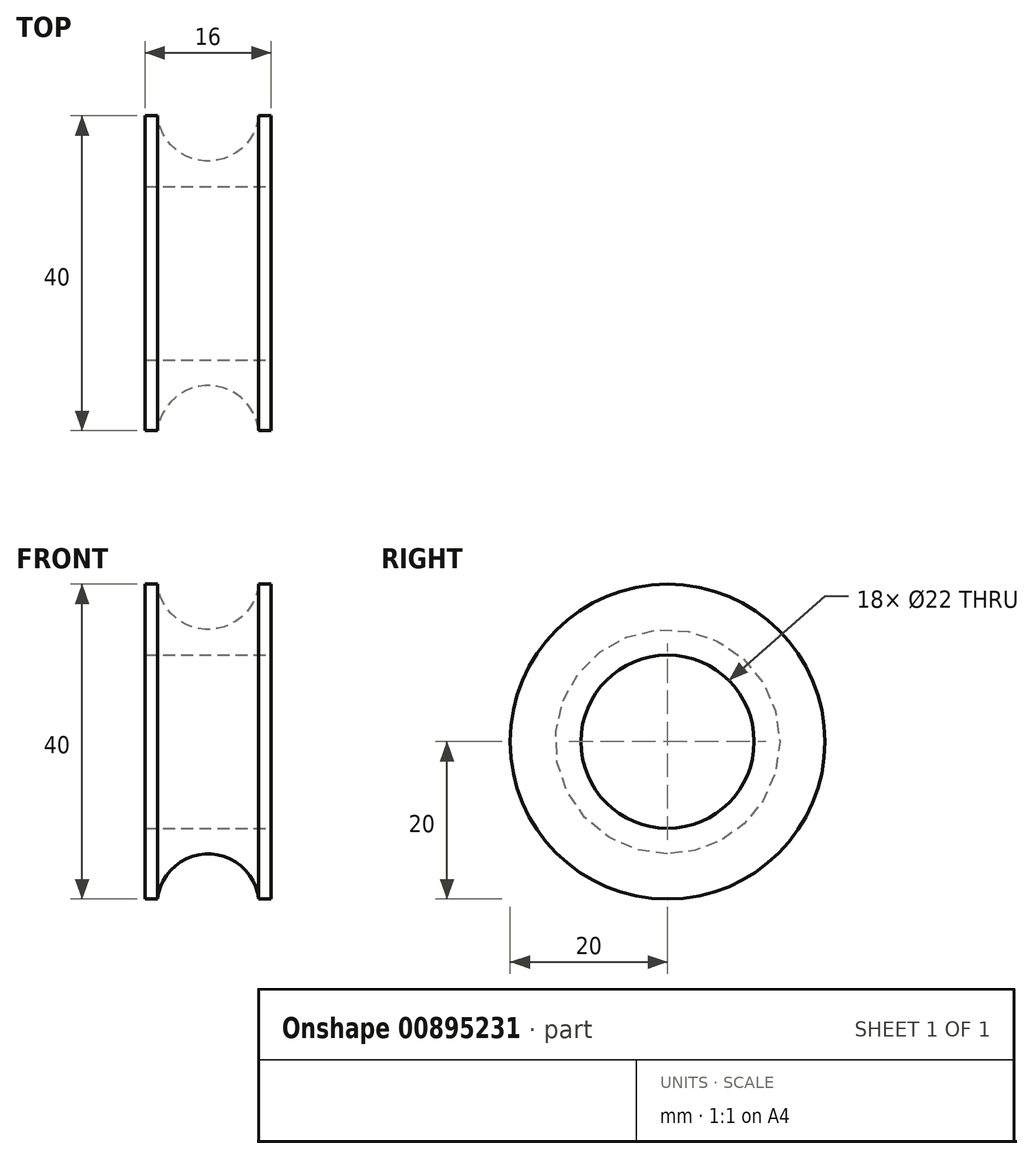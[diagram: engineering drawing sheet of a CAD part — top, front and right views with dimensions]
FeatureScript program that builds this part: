
annotation { "Feature Type Name" : "Feature", "Feature Type Description" : "" }
export const myFeature = defineFeature(function(context is Context, id is Id, definition is map)
    precondition{}
    {
        {
            var Q0;
            Q0=qCreatedBy(makeId("Front.planeOp"),FACE);
            var sketch = newSketch(context, id + "F0", { "sketchPlane" : qUnion([Q0])});
            skLineSegment(sketch, "E0", {"start": v(32.74, 0) * mm, "end": v(-36.5, 0) * mm, "construction": true});
            skLineSegment(sketch, "E1", {"start": v(0, 0) * mm, "end": v(-8, 0) * mm});
            skLineSegment(sketch, "E2", {"start": v(-8, 0) * mm, "end": v(-8, 20) * mm});
            skLineSegment(sketch, "E3", {"start": v(-8, 20) * mm, "end": v(0, 20) * mm});
            skLineSegment(sketch, "E4.MirrorCS", {"start": v(0, 0) * mm, "end": v(8, 0) * mm});
            skLineSegment(sketch, "E5.MirrorCS", {"start": v(8, 0) * mm, "end": v(8, 20) * mm});
            skLineSegment(sketch, "E6.MirrorCS", {"start": v(8, 20) * mm, "end": v(0, 20) * mm});
            skCircle(sketch, "E7", {"center": v(0, 20.74) * mm, "radius": 6.48 * mm});
            skSolve(sketch);
        }
        {
            var Q0;
            Q0=makeQuery(id+"F0.imprint","IMPRINT",FACE,{"disambiguationData":[TD([[makeQuery(id+"F0.imprint","IMPRINT",EDGE,{"derivedFrom":sQuery(id+"F0.wireOp",EDGE,"E1")}),-1.0]])]});
            var Q1;
            Q1=sQuery(id+"F0.wireOp",EDGE,"E0");
            revolve(context, id + "F1", {"surfaceOperationType" : NewSurfaceOperationType.NEW, "entities" : qUnion([Q0]), "axis" : qUnion([Q1]), "revolveType" : RevolveType.FULL});
        }
        {
            var Q0;
            Q0=makeQuery(id+"F1.opRevolve","SWEPT_FACE",FACE,{"disambiguationData":[OSD([sQuery(id+"F0.wireOp",EDGE,"E5.MirrorCS")])]});
            var sketch = newSketch(context, id + "F2", { "sketchPlane" : qUnion([Q0])});
            skCircle(sketch, "E8", {"center": v(0, 0) * mm, "radius": 11 * mm});
            skSolve(sketch);
        }
        {
            var Q0;
            Q0 = qSketchRegion(id + "F2", true);
            var Q1;
            Q1=makeQuery(id+"F2.imprint","IMPRINT",FACE,{"disambiguationData":[TD([[makeQuery(id+"F2.imprint","IMPRINT",EDGE,{"derivedFrom":sQuery(id+"F2.wireOp",EDGE,"E8")}),1.0]])]});
            extrude(context, id + "F3", {"entities" : qUnion([Q0, Q1]), "operationType" : NewBodyOperationType.REMOVE, "endBound" : BoundingType.THROUGH_ALL, "oppositeDirection" : true, "depth" : 25.4 * mm, "offsetDistance" : 25.4 * mm});
        }
    });
